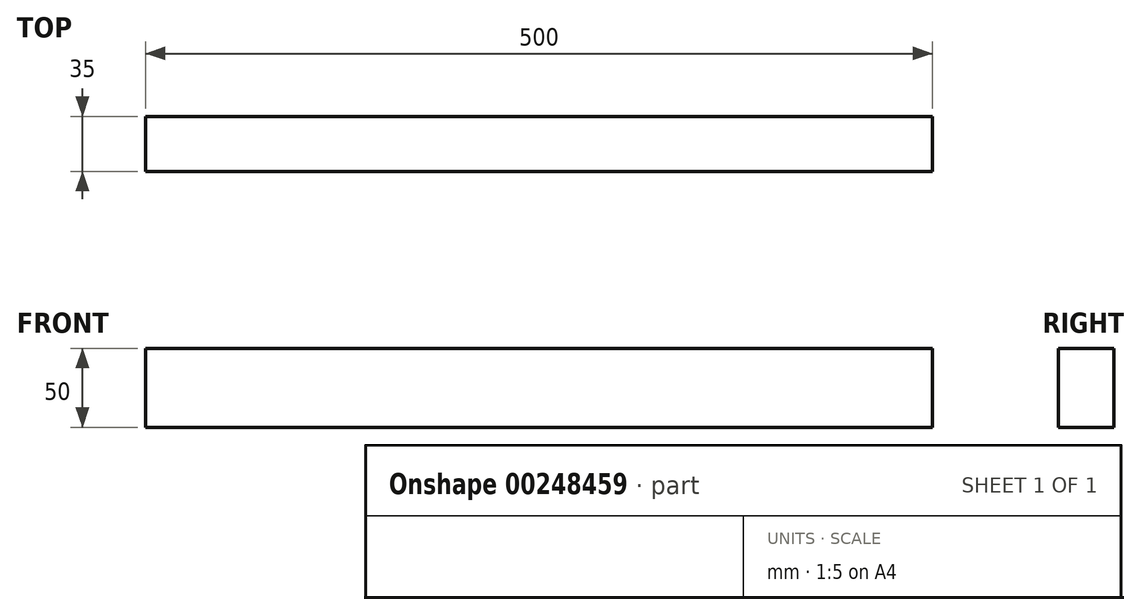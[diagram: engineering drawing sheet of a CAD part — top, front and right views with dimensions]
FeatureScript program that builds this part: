
annotation { "Feature Type Name" : "Feature", "Feature Type Description" : "" }
export const myFeature = defineFeature(function(context is Context, id is Id, definition is map)
    precondition{}
    {
        {
            var Q0;
            Q0=qCreatedBy(makeId("Right.planeOp"),FACE);
            var sketch = newSketch(context, id + "F0", { "sketchPlane" : qUnion([Q0])});
            skLineSegment(sketch, "E0.bottom", {"start": v(17.5, 25) * mm, "end": v(-17.5, 25) * mm});
            skLineSegment(sketch, "E0.top", {"start": v(17.5, -25) * mm, "end": v(-17.5, -25) * mm});
            skLineSegment(sketch, "E0.left", {"start": v(17.5, 25) * mm, "end": v(17.5, -25) * mm});
            skLineSegment(sketch, "E0.right", {"start": v(-17.5, 25) * mm, "end": v(-17.5, -25) * mm});
            skPoint(sketch, "E0.middle", {"position": v(0, 0) * mm});
            skSolve(sketch);
        }
        {
            var Q0;
            Q0=makeQuery(id+"F0.imprint","IMPRINT",FACE,{"disambiguationData":[TD([[makeQuery(id+"F0.imprint","IMPRINT",EDGE,{"derivedFrom":sQuery(id+"F0.wireOp",EDGE,"E0.bottom")}),1.0]])]});
            extrude(context, id + "F1", {"entities" : qUnion([Q0]), "endBound" : BoundingType.SYMMETRIC, "depth" : 500 * mm});
        }
    });
